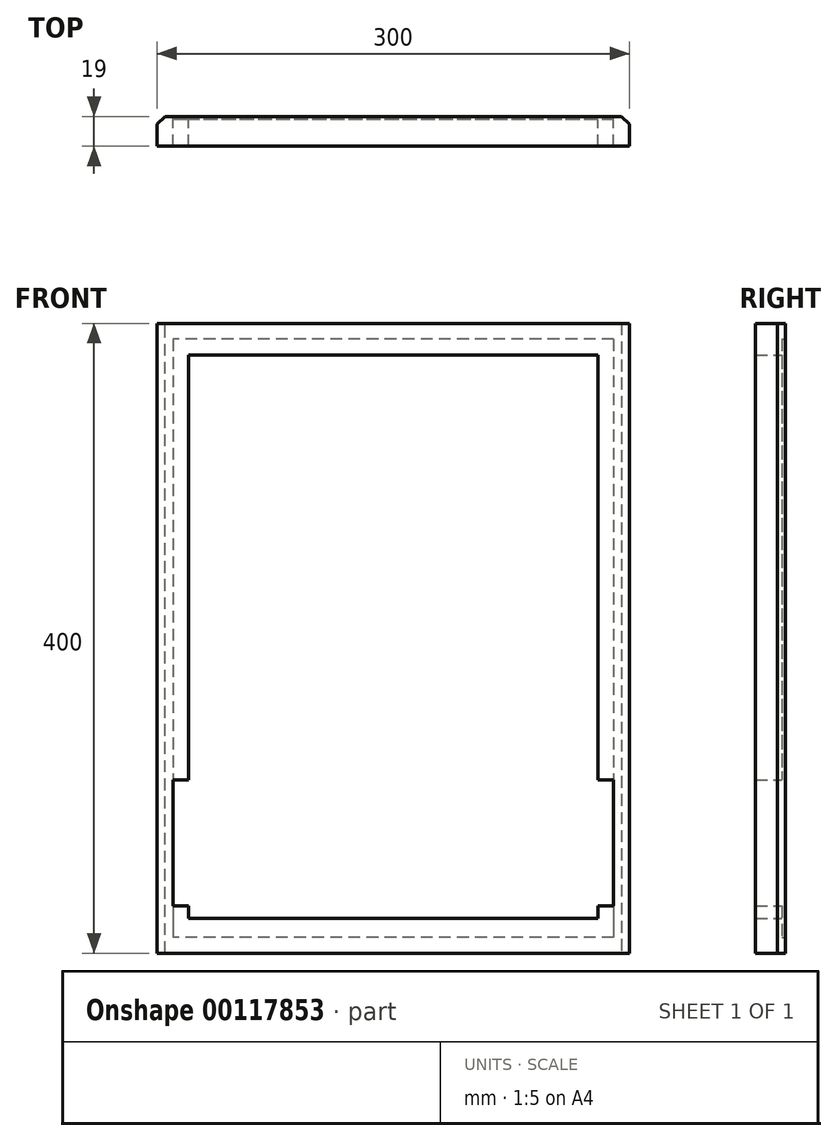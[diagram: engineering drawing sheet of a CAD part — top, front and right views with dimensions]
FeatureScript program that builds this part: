
annotation { "Feature Type Name" : "Feature", "Feature Type Description" : "" }
export const myFeature = defineFeature(function(context is Context, id is Id, definition is map)
    precondition{}
    {
        {
            var Q0;
            Q0=qCreatedBy(makeId("Front.planeOp"),FACE);
            var sketch = newSketch(context, id + "F0", { "sketchPlane" : qUnion([Q0])});
            skLineSegment(sketch, "E0.bottom", {"start": v(-181.72, 427.2) * mm, "end": v(118.28, 427.2) * mm});
            skLineSegment(sketch, "E0.top", {"start": v(-181.72, 27.2) * mm, "end": v(118.28, 27.2) * mm});
            skLineSegment(sketch, "E0.left", {"start": v(-181.72, 427.2) * mm, "end": v(-181.72, 27.2) * mm});
            skLineSegment(sketch, "E0.right", {"start": v(118.28, 427.2) * mm, "end": v(118.28, 27.2) * mm});
            skSolve(sketch);
        }
        {
            var Q0;
            Q0=makeQuery(id+"F0.imprint","IMPRINT",FACE,{"disambiguationData":[TD([[makeQuery(id+"F0.imprint","IMPRINT",EDGE,{"derivedFrom":sQuery(id+"F0.wireOp",EDGE,"E0.bottom")}),-1.0]])]});
            extrude(context, id + "F1", {"entities" : qUnion([Q0]), "depth" : 19 * mm});
        }
        {
            var Q0;
            Q0=makeQuery(id+"F1.opExtrude","CAP_FACE",FACE,{"disambiguationData":[OSD([sQuery(id+"F0.wireOp",EDGE,"E0.bottom"),sQuery(id+"F0.wireOp",EDGE,"E0.top"),sQuery(id+"F0.wireOp",EDGE,"E0.left"),sQuery(id+"F0.wireOp",EDGE,"E0.right")])],"isStart":true});
            var sketch = newSketch(context, id + "F2", { "sketchPlane" : qUnion([Q0])});
            skLineSegment(sketch, "E1.bottom", {"start": v(-108.28, 417.2) * mm, "end": v(171.72, 417.2) * mm});
            skLineSegment(sketch, "E1.top", {"start": v(-108.28, 37.2) * mm, "end": v(171.72, 37.2) * mm});
            skLineSegment(sketch, "E1.left", {"start": v(-108.28, 417.2) * mm, "end": v(-108.28, 37.2) * mm});
            skLineSegment(sketch, "E1.right", {"start": v(171.72, 417.2) * mm, "end": v(171.72, 37.2) * mm});
            skSolve(sketch);
        }
        {
            var Q0;
            Q0 = qSketchRegion(id + "F2", true);
            extrude(context, id + "F3", {"entities" : qUnion([Q0]), "operationType" : NewBodyOperationType.REMOVE, "oppositeDirection" : true, "depth" : 2 * mm});
        }
        {
            var Q0;
            Q0=makeQuery(id+"F3.boolean.opBoolean","COPY",FACE,{"derivedFrom":makeQuery(id+"F3.opExtrude","CAP_FACE",FACE,{"disambiguationData":[OSD([sQuery(id+"F2.wireOp",EDGE,"E1.bottom"),sQuery(id+"F2.wireOp",EDGE,"E1.top"),sQuery(id+"F2.wireOp",EDGE,"E1.left"),sQuery(id+"F2.wireOp",EDGE,"E1.right")])],"isStart":false})});
            var sketch = newSketch(context, id + "F4", { "sketchPlane" : qUnion([Q0])});
            skLineSegment(sketch, "E2.bottom", {"start": v(-98.28, 407.2) * mm, "end": v(161.72, 407.2) * mm});
            skLineSegment(sketch, "E2.top", {"start": v(-98.28, 49.2) * mm, "end": v(161.72, 49.2) * mm});
            skLineSegment(sketch, "E2.left", {"start": v(-98.28, 407.2) * mm, "end": v(-98.28, 49.2) * mm});
            skLineSegment(sketch, "E2.right", {"start": v(161.72, 407.2) * mm, "end": v(161.72, 49.2) * mm});
            skSolve(sketch);
        }
        {
            var Q0;
            Q0 = qSketchRegion(id + "F4", true);
            extrude(context, id + "F5", {"entities" : qUnion([Q0]), "operationType" : NewBodyOperationType.REMOVE, "oppositeDirection" : true, "depth" : 17 * mm});
        }
        {
            var Q0;
            Q0=makeQuery(id+"F1.opExtrude","CAP_EDGE",EDGE,{"disambiguationData":[OSD([sQuery(id+"F0.wireOp",EDGE,"E0.right")])],"isStart":true});
            var Q1;
            Q1=makeQuery(id+"F1.opExtrude","CAP_EDGE",EDGE,{"disambiguationData":[OSD([sQuery(id+"F0.wireOp",EDGE,"E0.left")])],"isStart":true});
            chamfer(context, id + "F6", {"entities" : qUnion([Q0, Q1]), "width" : 5 * mm, "tangentPropagation" : true});
        }
        {
            var Q0;
            Q0=makeQuery(id+"F3.boolean.opBoolean","COPY",FACE,{"derivedFrom":makeQuery(id+"F3.opExtrude","CAP_FACE",FACE,{"disambiguationData":[OSD([sQuery(id+"F2.wireOp",EDGE,"E1.bottom"),sQuery(id+"F2.wireOp",EDGE,"E1.top"),sQuery(id+"F2.wireOp",EDGE,"E1.left"),sQuery(id+"F2.wireOp",EDGE,"E1.right")])],"isStart":false})});
            var sketch = newSketch(context, id + "F7", { "sketchPlane" : qUnion([Q0])});
            skLineSegment(sketch, "E3.bottom", {"start": v(-108.28, 137.2) * mm, "end": v(-98.28, 137.2) * mm});
            skLineSegment(sketch, "E3.top", {"start": v(-108.28, 57.2) * mm, "end": v(-98.28, 57.2) * mm});
            skLineSegment(sketch, "E3.left", {"start": v(-108.28, 137.2) * mm, "end": v(-108.28, 57.2) * mm});
            skLineSegment(sketch, "E3.right", {"start": v(-98.28, 137.2) * mm, "end": v(-98.28, 57.2) * mm});
            skSolve(sketch);
        }
        {
            var Q0;
            Q0 = qSketchRegion(id + "F7", true);
            extrude(context, id + "F8", {"entities" : qUnion([Q0]), "operationType" : NewBodyOperationType.REMOVE, "oppositeDirection" : true, "depth" : 17 * mm});
        }
        {
            var Q0;
            Q0=makeQuery(id+"F3.boolean.opBoolean","COPY",FACE,{"derivedFrom":makeQuery(id+"F3.opExtrude","CAP_FACE",FACE,{"disambiguationData":[OSD([sQuery(id+"F2.wireOp",EDGE,"E1.bottom"),sQuery(id+"F2.wireOp",EDGE,"E1.top"),sQuery(id+"F2.wireOp",EDGE,"E1.left"),sQuery(id+"F2.wireOp",EDGE,"E1.right")])],"isStart":false})});
            var sketch = newSketch(context, id + "F9", { "sketchPlane" : qUnion([Q0])});
            skLineSegment(sketch, "E4.bottom", {"start": v(161.72, 137.2) * mm, "end": v(171.72, 137.2) * mm});
            skLineSegment(sketch, "E4.top", {"start": v(161.72, 57.2) * mm, "end": v(171.72, 57.2) * mm});
            skLineSegment(sketch, "E4.left", {"start": v(161.72, 137.2) * mm, "end": v(161.72, 57.2) * mm});
            skLineSegment(sketch, "E4.right", {"start": v(171.72, 137.2) * mm, "end": v(171.72, 57.2) * mm});
            skSolve(sketch);
        }
        {
            var Q0;
            Q0 = qSketchRegion(id + "F9", true);
            extrude(context, id + "F10", {"entities" : qUnion([Q0]), "operationType" : NewBodyOperationType.REMOVE, "oppositeDirection" : true, "depth" : 17 * mm});
        }
    });
